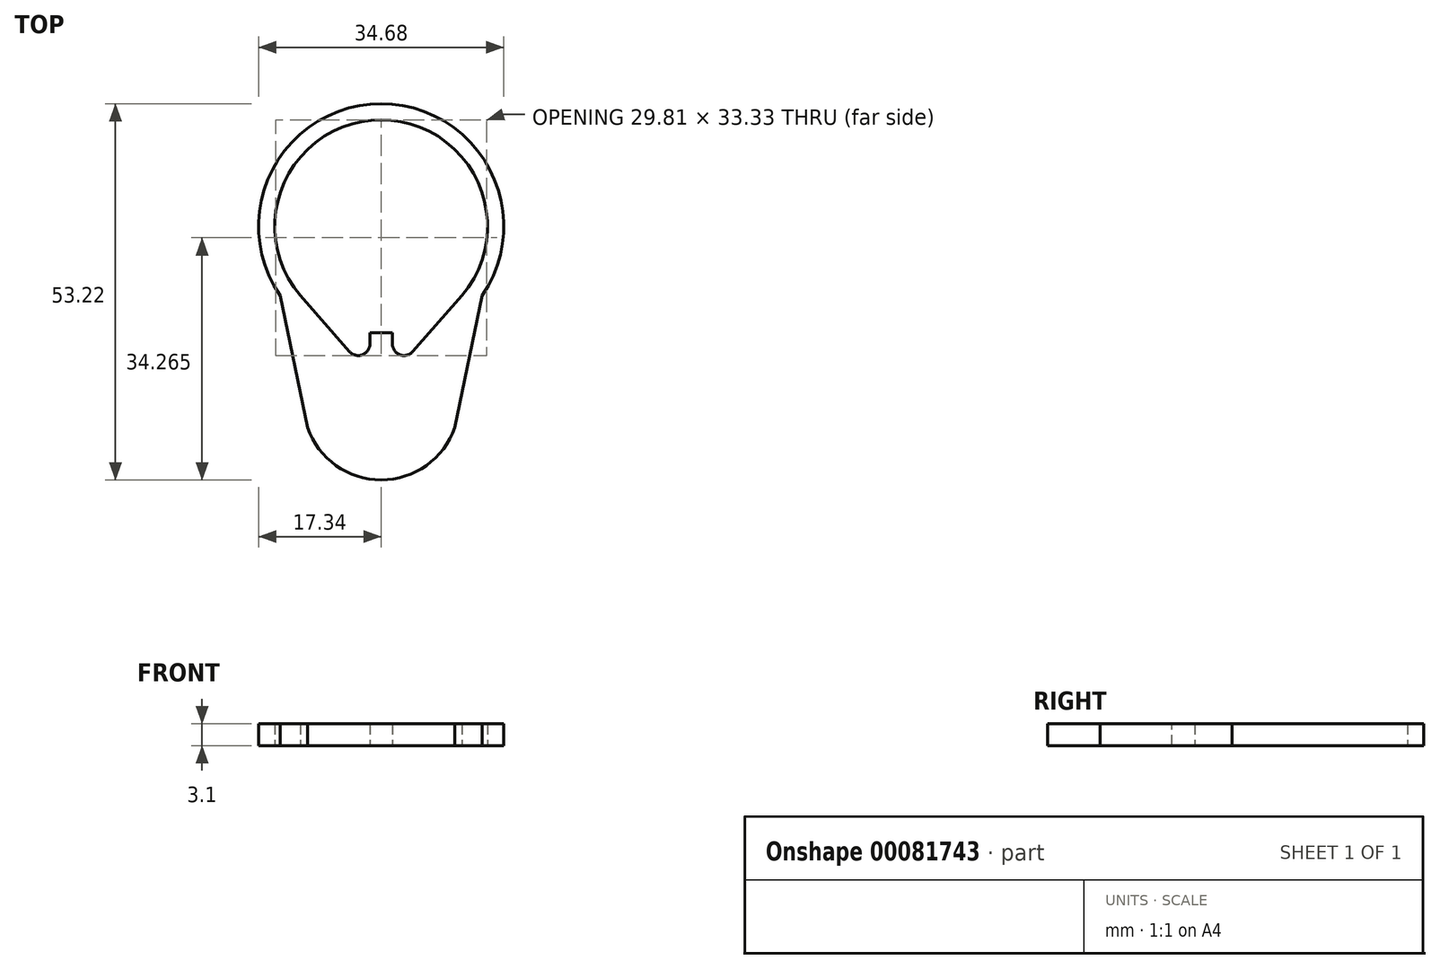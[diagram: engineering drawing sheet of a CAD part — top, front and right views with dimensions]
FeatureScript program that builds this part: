
annotation { "Feature Type Name" : "Feature", "Feature Type Description" : "" }
export const myFeature = defineFeature(function(context is Context, id is Id, definition is map)
    precondition{}
    {
        {
            var Q0;
            Q0=qCreatedBy(makeId("Top.planeOp"),FACE);
            var sketch = newSketch(context, id + "F0", { "sketchPlane" : qUnion([Q0])});
            skCircle(sketch, "E0", {"center": v(0, 0) * mm, "radius": 15.05 * mm, "construction": true});
            skLineSegment(sketch, "E1", {"start": v(0, 15.05) * mm, "end": v(0, -15.05) * mm, "construction": true});
            skLineSegment(sketch, "E2", {"start": v(-11.43, -9.79) * mm, "end": v(11.43, -9.79) * mm, "construction": true});
            skCircle(sketch, "E3", {"center": v(0, 0) * mm, "radius": 17.34 * mm, "construction": true});
            skLineSegment(sketch, "E4", {"start": v(-1.59, -15.05) * mm, "end": v(1.59, -15.05) * mm});
            skLineSegment(sketch, "E5", {"start": v(-14.3, -9.79) * mm, "end": v(-10.41, -28.44) * mm});
            skLineSegment(sketch, "E6", {"start": v(-10.41, -28.44) * mm, "end": v(10.41, -28.44) * mm, "construction": true});
            skLineSegment(sketch, "E7", {"start": v(0, -15.05) * mm, "end": v(0, -28.44) * mm, "construction": true});
            skLineSegment(sketch, "E8", {"start": v(10.41, -28.44) * mm, "end": v(14.3, -9.79) * mm});
            skLineSegment(sketch, "E9", {"start": v(0, -28.44) * mm, "end": v(0, -35.88) * mm, "construction": true});
            skArc(sketch, "E10", {"start": v(-10.41, -28.44) * mm, "mid": v(0, -35.88) * mm, "end": v(10.41, -28.44) * mm});
            skLineSegment(sketch, "E11", {"start": v(-3.81, -31.18) * mm, "end": v(0, -31.18) * mm, "construction": true});
            skLineSegment(sketch, "E12", {"start": v(0, -31.18) * mm, "end": v(3.81, -31.18) * mm, "construction": true});
            skLineSegment(sketch, "E13", {"start": v(-3.81, -21.02) * mm, "end": v(0, -21.02) * mm, "construction": true});
            skLineSegment(sketch, "E14", {"start": v(0, -21.02) * mm, "end": v(3.81, -21.02) * mm, "construction": true});
            skArc(sketch, "E15", {"start": v(-3.5, -20.78) * mm, "mid": v(-6.22, -25.9) * mm, "end": v(-3.81, -31.18) * mm, "construction": true});
            skArc(sketch, "E16", {"start": v(3.81, -31.18) * mm, "mid": v(6.22, -26.1) * mm, "end": v(3.81, -21.02) * mm, "construction": true});
            skLineSegment(sketch, "E17", {"start": v(-1.59, -15.05) * mm, "end": v(-1.59, -21.02) * mm});
            skLineSegment(sketch, "E18", {"start": v(1.59, -15.05) * mm, "end": v(1.59, -21.02) * mm});
            skArc(sketch, "E19", {"start": v(14.3, -9.79) * mm, "mid": v(0, 17.34) * mm, "end": v(-14.3, -9.79) * mm});
            skArc(sketch, "E20", {"start": v(11.43, -9.79) * mm, "mid": v(0, 15.05) * mm, "end": v(-11.43, -9.79) * mm});
            skLineSegment(sketch, "E21", {"start": v(-11.43, -9.79) * mm, "end": v(-1.59, -21.02) * mm});
            skLineSegment(sketch, "E22", {"start": v(1.59, -21.02) * mm, "end": v(11.43, -9.79) * mm});
            skLineSegment(sketch, "E23", {"start": v(-1.59, -16.83) * mm, "end": v(1.59, -16.83) * mm});
            skSolve(sketch);
        }
        {
            var Q0;
            Q0=makeQuery(id+"F0.imprint","IMPRINT",FACE,{"disambiguationData":[TD([[makeQuery(id+"F0.imprint","IMPRINT",EDGE,{"derivedFrom":sQuery(id+"F0.wireOp",EDGE,"E5")}),1.0]])]});
            extrude(context, id + "F1", {"entities" : qUnion([Q0]), "depth" : 3.1 * mm});
        }
        {
            var Q0;
            {var subQ0=sQuery(id+"F0.wireOp",EDGE,"E4");Q0=makeQuery(id+"F0.imprint","IMPRINT",FACE,{"disambiguationData":[TD([[makeQuery(id+"F0.imprint","IMPRINT",EDGE,{"derivedFrom":subQ0}),-1.0]])]});}
            extrude(context, id + "F2", {"entities" : qUnion([Q0]), "operationType" : NewBodyOperationType.ADD, "depth" : 3.1 * mm});
        }
        {
            var Q0;
            Q0=makeQuery(id+"F1.opExtrude","SWEPT_EDGE",EDGE,{"disambiguationData":[OSD([sQuery(id+"F0.wireOp",EDGE,"E17"),sQuery(id+"F0.wireOp",EDGE,"E21")])]});
            var Q1;
            Q1=makeQuery(id+"F1.opExtrude","SWEPT_EDGE",EDGE,{"disambiguationData":[OSD([sQuery(id+"F0.wireOp",EDGE,"E18"),sQuery(id+"F0.wireOp",EDGE,"E22")])]});
            fillet(context, id + "F3", {"entities" : qUnion([Q0, Q1]), "radius" : 1.65 * mm, "tangentPropagation" : true, "allowEdgeOverflow" : false});
        }
    });
